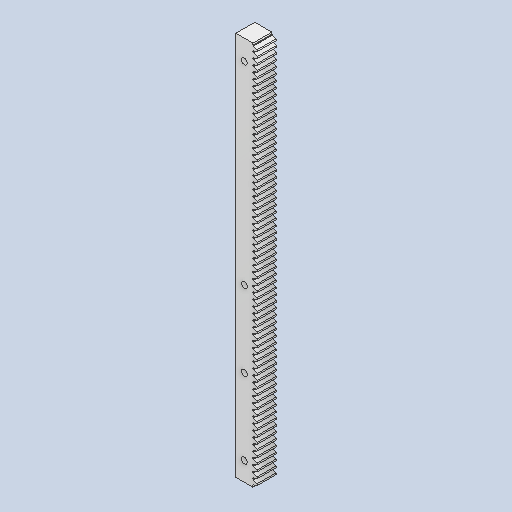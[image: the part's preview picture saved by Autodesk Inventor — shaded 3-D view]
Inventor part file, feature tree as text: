
AUTODESK INVENTOR PART (.ipt)
format: ipt  version: 2023 (Build 270158000, 158)  size: 2,996,224 bytes
history: native  units: mm
features: sketch x4, extrude x3, other x1, hole x1
ambient origin geometry x8: Origin, YZ Plane, XZ Plane, XY Plane, X Axis, Y Axis, Z Axis, Center Point
bodies: Body1 (feature_tree)
feature tree (9):
  other  "ソリッド1"
  extrude  "押し出し1"  Depth=10.0mm
  extrude  "押し出し12"  Depth=3.95363mm
  extrude  "押し出し13"  Depth=10.0mm
  hole  "穴3"  [1 undecoded]
  sketch  "スケッチ1"
  sketch  "スケッチ14"
  sketch  "スケッチ15"
  sketch  "スケッチ16"
note: 1 required parameter value undecoded (feature->parameter linkage not recoverable at this tier; creation-order binding heuristic only, values carry confidence <= 0.55)
